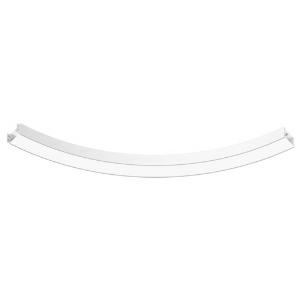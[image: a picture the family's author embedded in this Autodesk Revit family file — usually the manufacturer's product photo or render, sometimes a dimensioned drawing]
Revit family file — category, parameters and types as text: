
# Revit family: super-g_super-g__4000___72deg_ab_led__36_8w_5680lm_3000k_cri_80_350-1110_e132
name_source: partatom
category: Leuchten
revit_build: Autodesk Revit 2016 (Build: 20190508_0715(x64)
units: mm (PartAtom-declared; Revit-internal decimal feet)

## family parameters
Basisbauteil = Fläche
Beim Laden mit Abzugskörper schneiden = Nein
Bemaßung runder Anschluss = Durchmesser verwenden
Gemeinsam genutzt = Nein
Lichtquelle = Nein
Raumberechnungspunkt = Nein
Teiletyp = Normal

## types (1)
- 350-1110- (1 x LED, 710 lm, 3000K)
    Approval mark = CE
    Beschreibung = The insert consists of aluminum-extruded profile. Charming SOFT-EDGE design ensure unparalleled styling. The ballast is integrated and allows for an operation with 220-240V (50/60Hz). SUPER-G (# 350-1110) ist not dimmable (on/off).
    CIE Flux Codes = 44 75 94 100 65
    Color Rendering = 1B/80…89
    Color Temperature = 3000K
    Height = 120 mm
    Hersteller = Prolicht
    Lamp Light Flux = 710 lm
    Lamp count = 1
    Lampe = 1 x LED
    Length = 314 mm
    Luminous efficacy = 90 lm/W
    ModVariant = Nein
    Modell = 350-1110
    Mounting Place = Ceiling
    Mounting Type = Surface mounted
    Number of Poles = 1
    OnlyDefault = Ja
    Power Factor = 1
    Product Name = SUPER-G__SUPER-G  4000 / 72° AB LED: 36,8W 5680lm 3000K CRI:80
    Product group = Surface profile systems
    ProductGroupID = 335
    Protection Class = Protection class I
    Protection Degree = IP 20
    RLX_Detail_Level = 1
    RlxData = <blob elided: 29429 chars, md5=81259375>
    Scheinlast = 41 VA
    Socket = socket
    Standby Power = 0 W
    System Light Flux = 3692 lm
    System Power = 41 W
    Typenbild = 350-1110.jpg
    URL = http://relux.com
    VarID = 350-1110-
    Voltage = 0 V
    Vorgabe-Ansicht = 1800 mm
    Weight = 0.00 kg
    Width = 150 mm

## geometry (parser evidence)
native form markers: Blend x4, Sweep x30
no freeform markers — native parametric forms only
